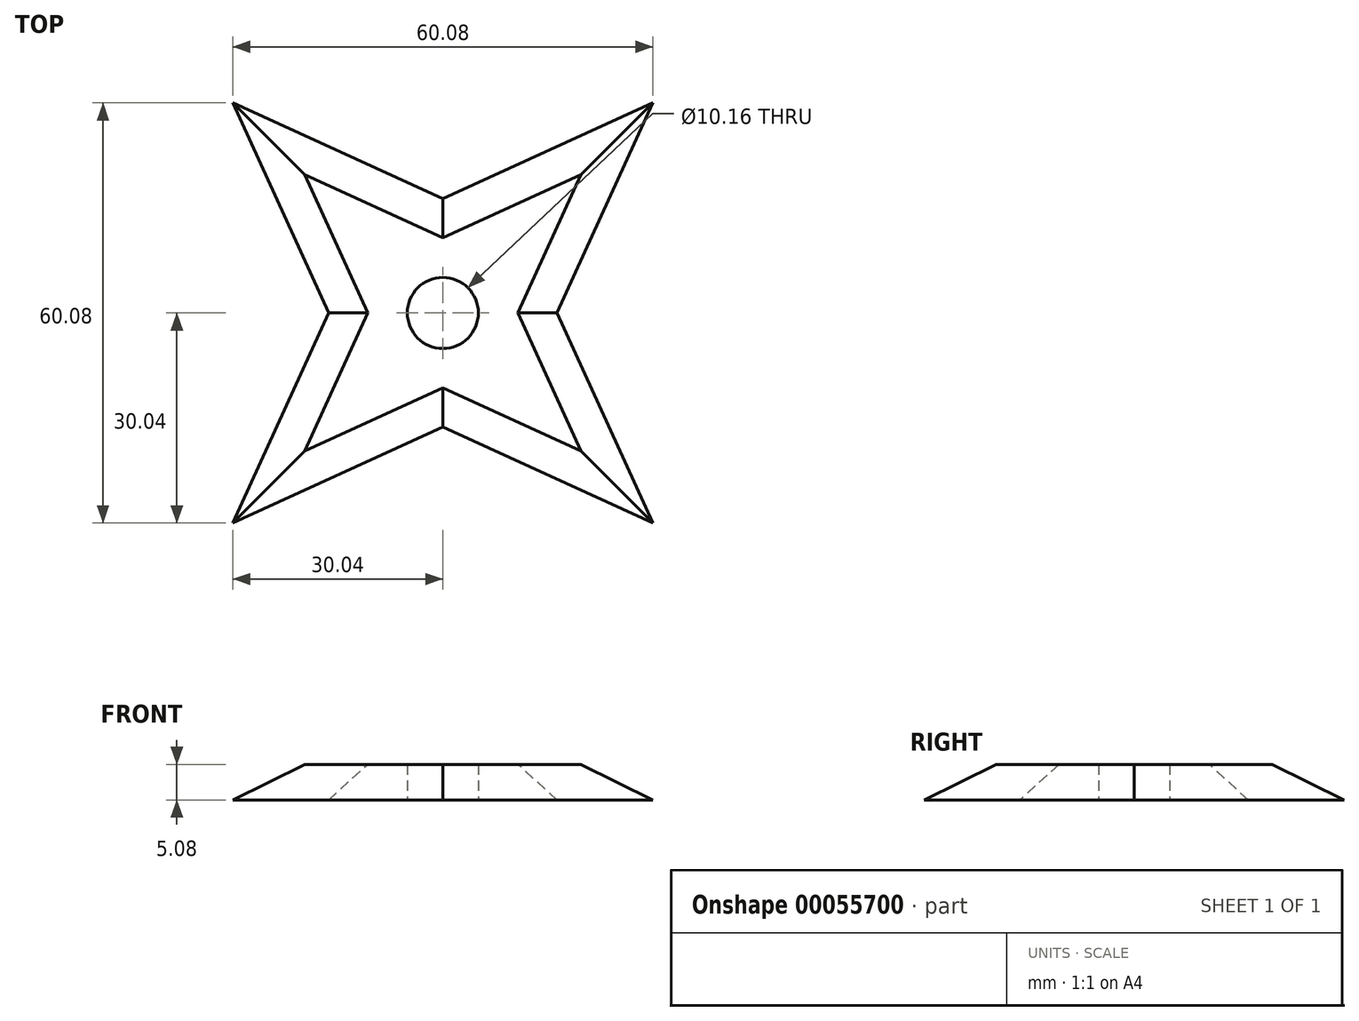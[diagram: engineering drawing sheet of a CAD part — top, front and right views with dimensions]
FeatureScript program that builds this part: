
annotation { "Feature Type Name" : "Feature", "Feature Type Description" : "" }
export const myFeature = defineFeature(function(context is Context, id is Id, definition is map)
    precondition{}
    {
        {
            var Q0;
            Q0=qCreatedBy(makeId("Top.planeOp"),FACE);
            var sketch = newSketch(context, id + "F0", { "sketchPlane" : qUnion([Q0])});
            skCircle(sketch, "E0", {"center": v(0, 0) * mm, "radius": 16.32 * mm});
            skLineSegment(sketch, "E1", {"start": v(0, 16.32) * mm, "end": v(30.04, 30.04) * mm});
            skLineSegment(sketch, "E2", {"start": v(30.04, 30.04) * mm, "end": v(16.32, 0) * mm});
            skLineSegment(sketch, "E3", {"start": v(16.32, 0) * mm, "end": v(30.04, -30.04) * mm});
            skLineSegment(sketch, "E4", {"start": v(-30.04, -30.04) * mm, "end": v(-16.32, 0) * mm});
            skLineSegment(sketch, "E5", {"start": v(-16.32, 0) * mm, "end": v(-30.04, 30.04) * mm});
            skLineSegment(sketch, "E6", {"start": v(-30.04, 30.04) * mm, "end": v(0, 16.32) * mm});
            skCircle(sketch, "E7", {"center": v(0, 0) * mm, "radius": 5.08 * mm});
            skLineSegment(sketch, "E8", {"start": v(0, -16.32) * mm, "end": v(-30.04, -30.04) * mm});
            skLineSegment(sketch, "E9", {"start": v(0, -16.32) * mm, "end": v(30.04, -30.04) * mm});
            skSolve(sketch);
        }
        {
            var Q0;
            {var subQ2=sQuery(id+"F0.wireOp",EDGE,"E5");Q0=makeQuery(id+"F0.imprint","IMPRINT",FACE,{"disambiguationData":[TD([[makeQuery(id+"F0.imprint","IMPRINT",EDGE,{"derivedFrom":subQ2}),-1.0]])]});}
            var Q1;
            {var subQ0=sQuery(id+"F0.wireOp",EDGE,"E1");Q1=makeQuery(id+"F0.imprint","IMPRINT",FACE,{"disambiguationData":[TD([[makeQuery(id+"F0.imprint","IMPRINT",EDGE,{"derivedFrom":subQ0}),-1.0]])]});}
            var Q2;
            {var subQ0=sQuery(id+"F0.wireOp",EDGE,"E3");Q2=makeQuery(id+"F0.imprint","IMPRINT",FACE,{"disambiguationData":[TD([[makeQuery(id+"F0.imprint","IMPRINT",EDGE,{"derivedFrom":subQ0}),-1.0]])]});}
            var Q3;
            {var subQ0=sQuery(id+"F0.wireOp",EDGE,"E4");Q3=makeQuery(id+"F0.imprint","IMPRINT",FACE,{"disambiguationData":[TD([[makeQuery(id+"F0.imprint","IMPRINT",EDGE,{"derivedFrom":subQ0}),-1.0]])]});}
            var Q4;
            Q4=makeQuery(id+"F0.imprint","IMPRINT",FACE,{"disambiguationData":[TD([[makeQuery(id+"F0.imprint","IMPRINT",EDGE,{"derivedFrom":sQuery(id+"F0.wireOp",EDGE,"E7")}),-1.0]])]});
            extrude(context, id + "F1", {"entities" : qUnion([Q0, Q1, Q2, Q3, Q4]), "depth" : 5.08 * mm});
        }
        {
            var Q0;
            Q0=makeQuery(id+"F1.opExtrude","CAP_EDGE",EDGE,{"disambiguationData":[OSD([sQuery(id+"F0.wireOp",EDGE,"E8")])],"isStart":false});
            var Q1;
            Q1=makeQuery(id+"F1.opExtrude","CAP_EDGE",EDGE,{"disambiguationData":[OSD([sQuery(id+"F0.wireOp",EDGE,"E4")])],"isStart":false});
            var Q2;
            Q2=makeQuery(id+"F1.opExtrude","CAP_EDGE",EDGE,{"disambiguationData":[OSD([sQuery(id+"F0.wireOp",EDGE,"E9")])],"isStart":false});
            var Q3;
            Q3=makeQuery(id+"F1.opExtrude","CAP_EDGE",EDGE,{"disambiguationData":[OSD([sQuery(id+"F0.wireOp",EDGE,"E3")])],"isStart":false});
            var Q4;
            Q4=makeQuery(id+"F1.opExtrude","CAP_EDGE",EDGE,{"disambiguationData":[OSD([sQuery(id+"F0.wireOp",EDGE,"E2")])],"isStart":false});
            var Q5;
            Q5=makeQuery(id+"F1.opExtrude","CAP_EDGE",EDGE,{"disambiguationData":[OSD([sQuery(id+"F0.wireOp",EDGE,"E1")])],"isStart":false});
            var Q6;
            Q6=makeQuery(id+"F1.opExtrude","CAP_EDGE",EDGE,{"disambiguationData":[OSD([sQuery(id+"F0.wireOp",EDGE,"E6")])],"isStart":false});
            var Q7;
            Q7=makeQuery(id+"F1.opExtrude","CAP_EDGE",EDGE,{"disambiguationData":[OSD([sQuery(id+"F0.wireOp",EDGE,"E5")])],"isStart":false});
            chamfer(context, id + "F2", {"entities" : qUnion([Q0, Q1, Q2, Q3, Q4, Q5, Q6, Q7]), "width" : 5.08 * mm, "tangentPropagation" : true});
        }
    });
